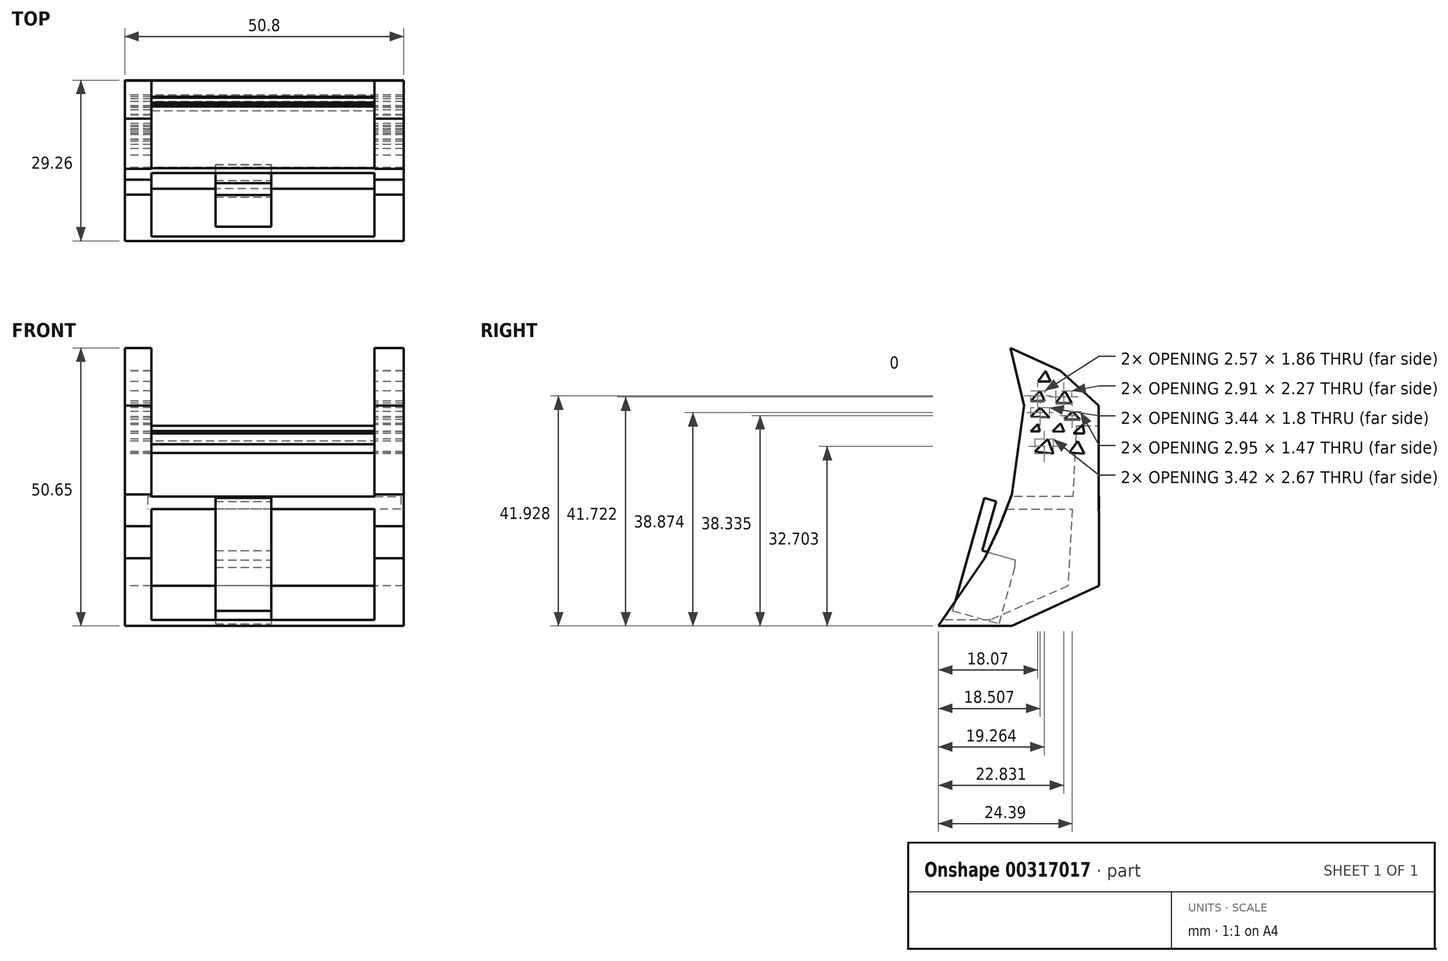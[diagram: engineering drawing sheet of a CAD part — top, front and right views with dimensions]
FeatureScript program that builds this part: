
annotation { "Feature Type Name" : "Feature", "Feature Type Description" : "" }
export const myFeature = defineFeature(function(context is Context, id is Id, definition is map)
    precondition{}
    {
        {
            var Q0;
            Q0=qCreatedBy(makeId("Right.planeOp"),FACE);
            var sketch = newSketch(context, id + "F0", { "sketchPlane" : qUnion([Q0])});
            skLineSegment(sketch, "E0", {"start": v(-38.03, 43.33) * mm, "end": v(-28.94, 39.22) * mm});
            skLineSegment(sketch, "E1", {"start": v(-28.94, 39.22) * mm, "end": v(-21.98, 32.81) * mm});
            skLineSegment(sketch, "E2", {"start": v(-21.98, 32.81) * mm, "end": v(-21.98, 16.67) * mm});
            skLineSegment(sketch, "E3", {"start": v(-21.98, 16.67) * mm, "end": v(-37.78, 16.67) * mm});
            skLineSegment(sketch, "E4", {"start": v(-37.78, 16.67) * mm, "end": v(-35.56, 32.81) * mm});
            skLineSegment(sketch, "E5", {"start": v(-35.56, 32.81) * mm, "end": v(-38.03, 43.33) * mm});
            skLineSegment(sketch, "E6", {"start": v(-51.18, -7.32) * mm, "end": v(-37.78, -7.32) * mm});
            skLineSegment(sketch, "E7", {"start": v(-37.78, -7.32) * mm, "end": v(-21.94, 0) * mm});
            skLineSegment(sketch, "E8", {"start": v(-33.01, 37.2) * mm, "end": v(-31.6, 39.14) * mm});
            skLineSegment(sketch, "E9", {"start": v(-31.6, 39.14) * mm, "end": v(-30.74, 37.2) * mm});
            skLineSegment(sketch, "E10", {"start": v(-30.74, 37.2) * mm, "end": v(-33.01, 37.2) * mm});
            skLineSegment(sketch, "E11", {"start": v(-34.4, 33.68) * mm, "end": v(-32.63, 35.54) * mm});
            skLineSegment(sketch, "E12", {"start": v(-32.63, 35.54) * mm, "end": v(-31.83, 33.68) * mm});
            skLineSegment(sketch, "E13", {"start": v(-31.83, 33.68) * mm, "end": v(-34.4, 33.68) * mm});
            skLineSegment(sketch, "E14", {"start": v(-29.8, 33.27) * mm, "end": v(-28.16, 35.54) * mm});
            skLineSegment(sketch, "E15", {"start": v(-28.16, 35.54) * mm, "end": v(-26.9, 33.27) * mm});
            skLineSegment(sketch, "E16", {"start": v(-26.9, 33.27) * mm, "end": v(-29.8, 33.27) * mm});
            skLineSegment(sketch, "E17", {"start": v(-34.4, 30.82) * mm, "end": v(-32.63, 32.46) * mm});
            skLineSegment(sketch, "E18", {"start": v(-32.63, 32.46) * mm, "end": v(-30.95, 30.65) * mm});
            skLineSegment(sketch, "E19", {"start": v(-30.95, 30.65) * mm, "end": v(-34.4, 30.82) * mm});
            skLineSegment(sketch, "E20", {"start": v(-28.26, 30.28) * mm, "end": v(-26.74, 31.75) * mm});
            skLineSegment(sketch, "E21", {"start": v(-26.74, 31.75) * mm, "end": v(-25.32, 30.28) * mm});
            skLineSegment(sketch, "E22", {"start": v(-25.32, 30.28) * mm, "end": v(-28.26, 30.28) * mm});
            skLineSegment(sketch, "E23", {"start": v(-30.38, 28.14) * mm, "end": v(-28.88, 29.6) * mm});
            skLineSegment(sketch, "E24", {"start": v(-28.88, 29.6) * mm, "end": v(-28.26, 28.05) * mm});
            skLineSegment(sketch, "E25", {"start": v(-28.26, 28.05) * mm, "end": v(-30.38, 28.14) * mm});
            skLineSegment(sketch, "E26", {"start": v(-34.4, 28.14) * mm, "end": v(-33.01, 29.47) * mm});
            skLineSegment(sketch, "E27", {"start": v(-33.01, 29.47) * mm, "end": v(-32.7, 28.14) * mm});
            skLineSegment(sketch, "E28", {"start": v(-32.7, 28.14) * mm, "end": v(-34.4, 28.14) * mm});
            skLineSegment(sketch, "E29", {"start": v(-26.57, 27.73) * mm, "end": v(-24.93, 29.32) * mm});
            skLineSegment(sketch, "E30", {"start": v(-24.93, 29.32) * mm, "end": v(-24.56, 27.73) * mm});
            skLineSegment(sketch, "E31", {"start": v(-24.56, 27.73) * mm, "end": v(-26.57, 27.73) * mm});
            skLineSegment(sketch, "E32", {"start": v(-33.63, 24.44) * mm, "end": v(-31.27, 26.72) * mm});
            skLineSegment(sketch, "E33", {"start": v(-31.27, 26.72) * mm, "end": v(-30.2, 24.05) * mm});
            skLineSegment(sketch, "E34", {"start": v(-30.2, 24.05) * mm, "end": v(-33.63, 24.44) * mm});
            skLineSegment(sketch, "E35", {"start": v(-27.32, 24.24) * mm, "end": v(-25.8, 26.36) * mm});
            skPoint(sketch, "E35.startSnap0", {"position": v(-31.92, 24.24) * mm});
            skLineSegment(sketch, "E36", {"start": v(-25.8, 26.36) * mm, "end": v(-24.56, 24.08) * mm});
            skLineSegment(sketch, "E37", {"start": v(-24.56, 24.08) * mm, "end": v(-27.32, 24.24) * mm});
            skLineSegment(sketch, "E38", {"start": v(-40.03, 10.85) * mm, "end": v(-21.94, 10.85) * mm});
            skLineSegment(sketch, "E39", {"start": v(-21.94, 10.85) * mm, "end": v(-21.94, 5.04) * mm});
            skLineSegment(sketch, "E40", {"start": v(-21.94, 5.04) * mm, "end": v(-42.72, 5.04) * mm});
            skLineSegment(sketch, "E41", {"start": v(-37.78, 16.67) * mm, "end": v(-40.03, 10.85) * mm});
            skLineSegment(sketch, "E42", {"start": v(-40.03, 10.85) * mm, "end": v(-42.72, 5.04) * mm});
            skLineSegment(sketch, "E43", {"start": v(-42.72, 5.04) * mm, "end": v(-46.17, 0) * mm});
            skLineSegment(sketch, "E44", {"start": v(-46.17, 0) * mm, "end": v(-51.18, -7.32) * mm});
            skLineSegment(sketch, "E45", {"start": v(-21.98, 16.67) * mm, "end": v(-21.94, 10.85) * mm});
            skLineSegment(sketch, "E46", {"start": v(-21.94, 5.04) * mm, "end": v(-21.94, 0) * mm});
            skLineSegment(sketch, "E47", {"start": v(-21.94, 0) * mm, "end": v(-46.17, 0) * mm});
            skSolve(sketch);
        }
        {
            var Q0;
            Q0 = qSketchRegion(id + "F0", true);
            extrude(context, id + "F1", {"entities" : qUnion([Q0]), "depth" : 50.8 * mm});
        }
        {
            var Q0;
            Q0=qCreatedBy(makeId("Right.planeOp"),FACE);
            var sketch = newSketch(context, id + "F2", { "sketchPlane" : qUnion([Q0])});
            skLineSegment(sketch, "E48", {"start": v(-35.75, 32.99) * mm, "end": v(-25.81, 32.99) * mm});
            skLineSegment(sketch, "E49", {"start": v(-25.81, 32.99) * mm, "end": v(-27.54, 0) * mm});
            skLineSegment(sketch, "E50", {"start": v(-27.54, 0) * mm, "end": v(-41.66, -6.18) * mm});
            skLineSegment(sketch, "E51", {"start": v(-41.66, -6.18) * mm, "end": v(-54.76, -6.18) * mm});
            skLineSegment(sketch, "E52", {"start": v(-54.76, -6.18) * mm, "end": v(-54.76, 32.99) * mm});
            skLineSegment(sketch, "E53", {"start": v(-54.76, 32.99) * mm, "end": v(-35.75, 32.99) * mm});
            skSolve(sketch);
        }
        {
            var Q0;
            Q0 = qSketchRegion(id + "F2", true);
            extrude(context, id + "F3", {"entities" : qUnion([Q0]), "operationType" : NewBodyOperationType.REMOVE, "depth" : 45.47 * mm, "hasSecondDirection" : true, "secondDirectionOppositeDirection" : false, "secondDirectionDepth" : 4.83 * mm});
        }
        {
            var Q0;
            Q0=qCreatedBy(makeId("Right.planeOp"),FACE);
            var sketch = newSketch(context, id + "F4", { "sketchPlane" : qUnion([Q0])});
            skLineSegment(sketch, "E54", {"start": v(-42.36, 45.75) * mm, "end": v(-42.36, 29.14) * mm});
            skLineSegment(sketch, "E55", {"start": v(-17.65, 29.14) * mm, "end": v(-17.65, 45.75) * mm});
            skLineSegment(sketch, "E56", {"start": v(-17.65, 45.75) * mm, "end": v(-42.36, 45.75) * mm});
            skLineSegment(sketch, "E57", {"start": v(-42.36, 29.14) * mm, "end": v(-17.65, 29.14) * mm});
            skSolve(sketch);
        }
        {
            var Q0;
            Q0 = qSketchRegion(id + "F4", true);
            extrude(context, id + "F5", {"entities" : qUnion([Q0]), "operationType" : NewBodyOperationType.REMOVE, "depth" : 45.47 * mm, "hasSecondDirection" : true, "secondDirectionOppositeDirection" : false, "secondDirectionDepth" : 4.83 * mm});
        }
        {
            var Q0;
            Q0=qCreatedBy(makeId("Right.planeOp"),FACE);
            var sketch = newSketch(context, id + "F6", { "sketchPlane" : qUnion([Q0])});
            skLineSegment(sketch, "E58", {"start": v(-37.93, 16.28) * mm, "end": v(-21.92, 16.28) * mm});
            skLineSegment(sketch, "E59", {"start": v(-21.92, 16.28) * mm, "end": v(-21.92, 13.96) * mm});
            skLineSegment(sketch, "E60", {"start": v(-21.92, 13.96) * mm, "end": v(-38.82, 13.96) * mm});
            skLineSegment(sketch, "E61", {"start": v(-38.82, 13.96) * mm, "end": v(-37.93, 16.28) * mm});
            skSolve(sketch);
        }
        {
            var Q0;
            Q0 = qSketchRegion(id + "F6", true);
            extrude(context, id + "F7", {"entities" : qUnion([Q0]), "operationType" : NewBodyOperationType.ADD, "depth" : 50.3 * mm, "hasSecondDirection" : true, "secondDirectionOppositeDirection" : false, "secondDirectionDepth" : 4.17 * mm});
        }
        {
            var Q0;
            Q0=qCreatedBy(makeId("Right.planeOp"),FACE);
            var sketch = newSketch(context, id + "F8", { "sketchPlane" : qUnion([Q0])});
            skLineSegment(sketch, "E62", {"start": v(53.66, 36.69) * mm, "end": v(53.66, 58.03) * mm});
            skLineSegment(sketch, "E63", {"start": v(53.66, 47.36) * mm, "end": v(44.93, 47.36) * mm});
            skLineSegment(sketch, "E64", {"start": v(44.93, 47.36) * mm, "end": v(44.93, 36.69) * mm});
            skLineSegment(sketch, "E65", {"start": v(53.66, 58.03) * mm, "end": v(51.43, 58.03) * mm});
            skLineSegment(sketch, "E66", {"start": v(51.43, 58.03) * mm, "end": v(51.43, 48.68) * mm});
            skLineSegment(sketch, "E67", {"start": v(51.43, 48.68) * mm, "end": v(45.23, 48.68) * mm});
            skLineSegment(sketch, "E68", {"start": v(45.23, 48.68) * mm, "end": v(44.93, 47.36) * mm});
            skLineSegment(sketch, "E69", {"start": v(44.93, 36.69) * mm, "end": v(48.26, 36.69) * mm});
            skLineSegment(sketch, "E70", {"start": v(48.26, 36.69) * mm, "end": v(48.26, 47.36) * mm});
            skLineSegment(sketch, "E71", {"start": v(53.66, 36.69) * mm, "end": v(50.85, 36.69) * mm});
            skLineSegment(sketch, "E72", {"start": v(50.85, 36.69) * mm, "end": v(50.85, 47.36) * mm});
            skLineSegment(sketch, "E73", {"start": v(50.85, 47.36) * mm, "end": v(50.85, 36.69) * mm});
            skLineSegment(sketch, "E74", {"start": v(48.26, 36.69) * mm, "end": v(50.85, 36.69) * mm});
            skSolve(sketch);
        }
        {
            var Q0;
            Q0 = qSketchRegion(id + "F8", true);
            extrude(context, id + "F9", {"entities" : qUnion([Q0]), "depth" : 10.16 * mm});
        }
        {
            var Q0;
            Q0=makeQuery(id+"F9.opExtrude","SWEPT_BODY",BODY,{"disambiguationData":[OSD([sQuery(id+"F8.wireOp",EDGE,"E62"),sQuery(id+"F8.wireOp",EDGE,"E64"),sQuery(id+"F8.wireOp",EDGE,"E65"),sQuery(id+"F8.wireOp",EDGE,"E66"),sQuery(id+"F8.wireOp",EDGE,"E67"),sQuery(id+"F8.wireOp",EDGE,"E68"),sQuery(id+"F8.wireOp",EDGE,"E69"),sQuery(id+"F8.wireOp",EDGE,"E71"),sQuery(id+"F8.wireOp",EDGE,"E74")])]});
            transform(context, id + "F10", {"entities" : qUnion([Q0]), "transformType" : TransformType.TRANSLATION_3D, "dx" : 13.46 * mm, "dy" : -95.76 * mm, "dz" : -42.42 * mm, "makeCopy" : false});
        }
        {
            var Q0;
            Q0=makeQuery(id+"F9.opExtrude","SWEPT_BODY",BODY,{"disambiguationData":[OSD([sQuery(id+"F8.wireOp",EDGE,"E62"),sQuery(id+"F8.wireOp",EDGE,"E64"),sQuery(id+"F8.wireOp",EDGE,"E65"),sQuery(id+"F8.wireOp",EDGE,"E66"),sQuery(id+"F8.wireOp",EDGE,"E67"),sQuery(id+"F8.wireOp",EDGE,"E68"),sQuery(id+"F8.wireOp",EDGE,"E69"),sQuery(id+"F8.wireOp",EDGE,"E71"),sQuery(id+"F8.wireOp",EDGE,"E74")])]});
            var Q1;
            Q1=makeQuery(id+"F1.opExtrude","CAP_EDGE",EDGE,{"disambiguationData":[OSD([sQuery(id+"F0.wireOp",EDGE,"E4")])],"isStart":false});
            transform(context, id + "F11", {"entities" : qUnion([Q0]), "transformType" : TransformType.ROTATION, "transformAxis" : qUnion([Q1]), "angle" : 180 * degree, "makeCopy" : false});
        }
        {
            var Q0;
            Q0=makeQuery(id+"F9.opExtrude","SWEPT_BODY",BODY,{"disambiguationData":[OSD([sQuery(id+"F8.wireOp",EDGE,"E62"),sQuery(id+"F8.wireOp",EDGE,"E64"),sQuery(id+"F8.wireOp",EDGE,"E65"),sQuery(id+"F8.wireOp",EDGE,"E66"),sQuery(id+"F8.wireOp",EDGE,"E67"),sQuery(id+"F8.wireOp",EDGE,"E68"),sQuery(id+"F8.wireOp",EDGE,"E69"),sQuery(id+"F8.wireOp",EDGE,"E71"),sQuery(id+"F8.wireOp",EDGE,"E74")])]});
            transform(context, id + "F12", {"entities" : qUnion([Q0]), "transformType" : TransformType.TRANSLATION_3D, "dx" : -60.96 * mm, "dy" : -9.65 * mm, "dz" : 1.52 * mm, "makeCopy" : false});
        }
        {
            var Q0;
            Q0=makeQuery(id+"F9.opExtrude","SWEPT_BODY",BODY,{"disambiguationData":[OSD([sQuery(id+"F8.wireOp",EDGE,"E62"),sQuery(id+"F8.wireOp",EDGE,"E64"),sQuery(id+"F8.wireOp",EDGE,"E65"),sQuery(id+"F8.wireOp",EDGE,"E66"),sQuery(id+"F8.wireOp",EDGE,"E67"),sQuery(id+"F8.wireOp",EDGE,"E68"),sQuery(id+"F8.wireOp",EDGE,"E69"),sQuery(id+"F8.wireOp",EDGE,"E71"),sQuery(id+"F8.wireOp",EDGE,"E74")])]});
            transform(context, id + "F13", {"entities" : qUnion([Q0]), "transformType" : TransformType.TRANSLATION_3D, "dx" : -0.5 * mm, "dy" : 0.76 * mm, "dz" : 0 * mm, "makeCopy" : false});
        }
    });
